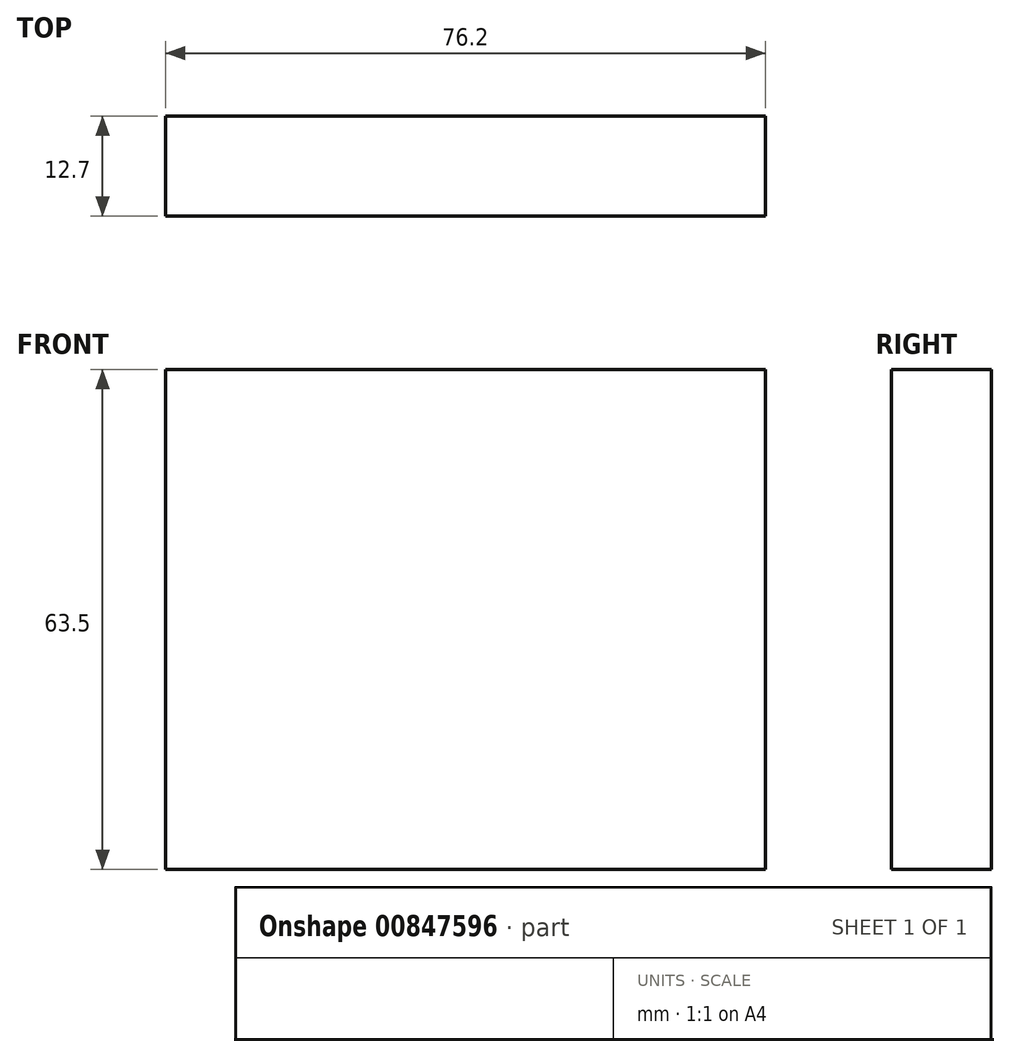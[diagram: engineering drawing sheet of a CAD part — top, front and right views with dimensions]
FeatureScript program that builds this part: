
annotation { "Feature Type Name" : "Feature", "Feature Type Description" : "" }
export const myFeature = defineFeature(function(context is Context, id is Id, definition is map)
    precondition{}
    {
        {
            var Q0;
            Q0=qCreatedBy(makeId("Front.planeOp"),FACE);
            var sketch = newSketch(context, id + "F0", { "sketchPlane" : qUnion([Q0])});
            skLineSegment(sketch, "E0.bottom", {"start": v(8.9, -9.14) * mm, "end": v(-67.3, -9.14) * mm});
            skLineSegment(sketch, "E0.top", {"start": v(8.9, 54.36) * mm, "end": v(-67.3, 54.36) * mm});
            skLineSegment(sketch, "E0.left", {"start": v(8.9, -9.14) * mm, "end": v(8.9, 54.36) * mm});
            skLineSegment(sketch, "E0.right", {"start": v(-67.3, -9.14) * mm, "end": v(-67.3, 54.36) * mm});
            skPoint(sketch, "E0.middle", {"position": v(-29.2, 22.61) * mm});
            skSolve(sketch);
        }
        {
            var Q0;
            Q0 = qSketchRegion(id + "F0", true);
            extrude(context, id + "F1", {"entities" : qUnion([Q0]), "depth" : 12.7 * mm, "offsetDistance" : 25.4 * mm});
        }
    });
